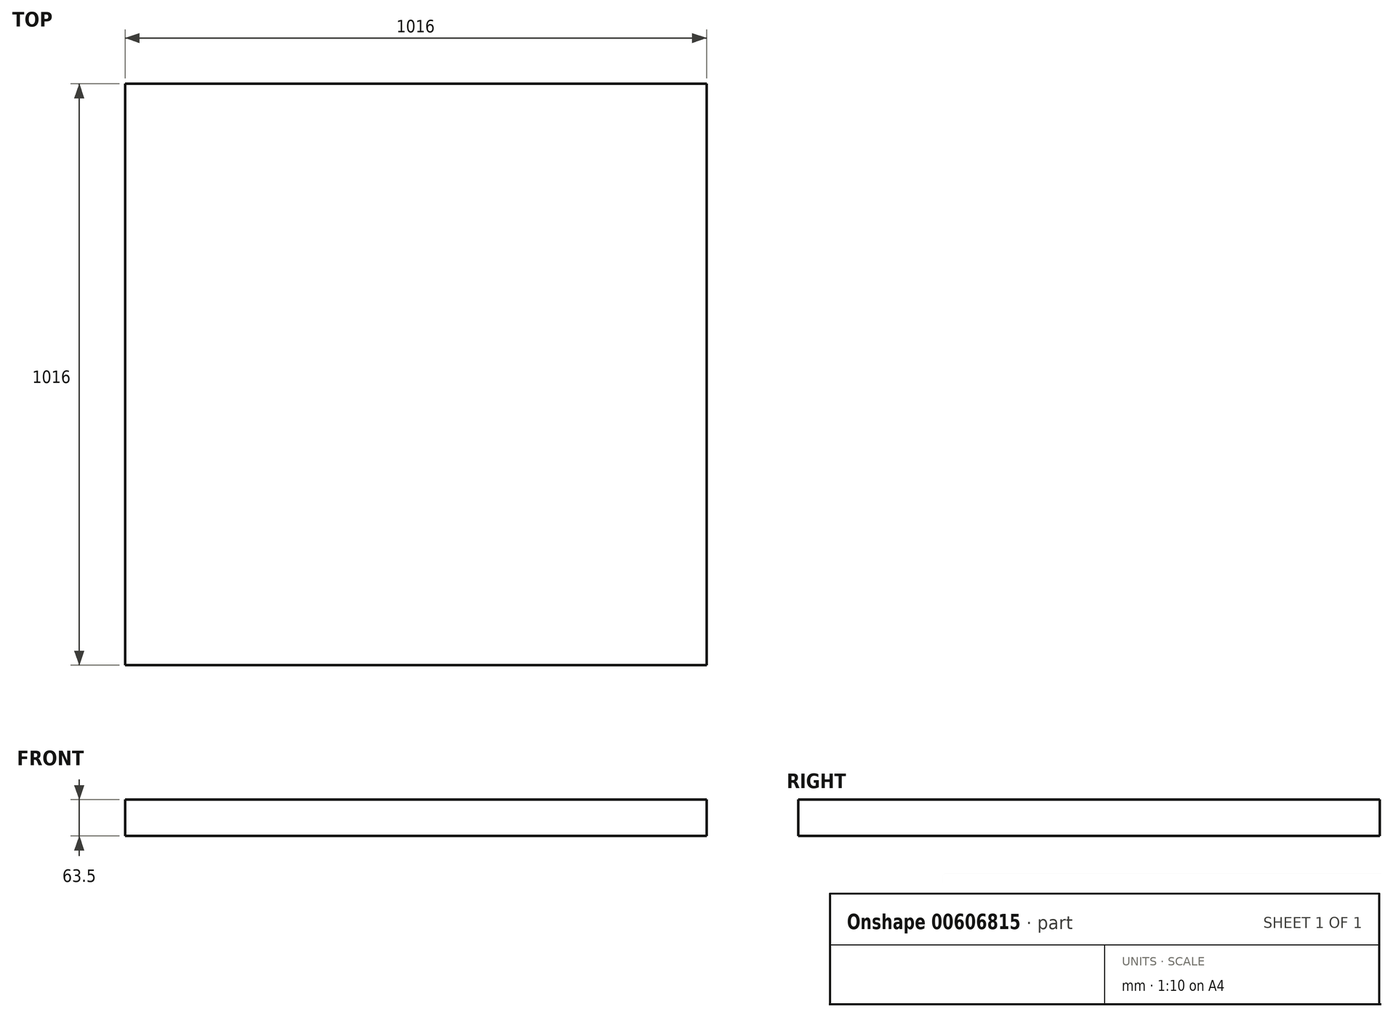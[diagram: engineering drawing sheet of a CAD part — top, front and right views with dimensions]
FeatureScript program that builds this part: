
annotation { "Feature Type Name" : "Feature", "Feature Type Description" : "" }
export const myFeature = defineFeature(function(context is Context, id is Id, definition is map)
    precondition{}
    {
        {
            var Q0;
            Q0=qCreatedBy(makeId("Top.planeOp"),FACE);
            var sketch = newSketch(context, id + "F0", { "sketchPlane" : qUnion([Q0])});
            skLineSegment(sketch, "E0.bottom", {"start": v(508, 508) * mm, "end": v(-508, 508) * mm});
            skLineSegment(sketch, "E0.top", {"start": v(508, -508) * mm, "end": v(-508, -508) * mm});
            skLineSegment(sketch, "E0.left", {"start": v(508, 508) * mm, "end": v(508, -508) * mm});
            skLineSegment(sketch, "E0.right", {"start": v(-508, 508) * mm, "end": v(-508, -508) * mm});
            skPoint(sketch, "E0.middle", {"position": v(0, 0) * mm});
            skSolve(sketch);
        }
        {
            var Q0;
            Q0 = qSketchRegion(id + "F0", true);
            extrude(context, id + "F1", {"entities" : qUnion([Q0]), "depth" : 63.5 * mm, "offsetDistance" : 25.4 * mm});
        }
    });
